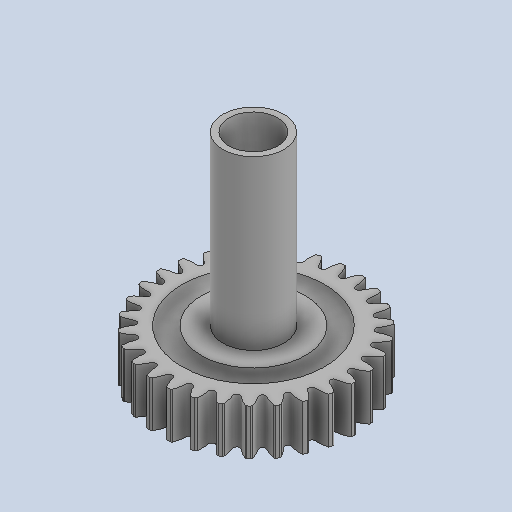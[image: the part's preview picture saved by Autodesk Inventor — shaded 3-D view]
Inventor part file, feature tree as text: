
AUTODESK INVENTOR PART (.ipt)
format: ipt  version: 2024 (Build 280153000, 153)  size: 743,936 bytes
history: native  units: mm
features: extrude x5, sketch x4, pattern_circular x2, fillet x1, revolve x1, plane x1, mirror x1, other x1, projected_geometry x1
ambient origin geometry x8: Origin, YZ Plane, XZ Plane, XY Plane, X Axis, Y Axis, Z Axis, Center Point
bodies: Body1 (feature_tree), Body2 (feature_tree)
feature tree (17):
  sketch  "Sketch4"  dims[d10=15.0mm d11=0.0mm d12=0.0mm d13=0.0mm]
  extrude  "Extrusion4"  TaperAngle=0.0deg  [1 undecoded]
  extrude  "Extrusion5"  Depth=0.5mm
  pattern_circular  "Circular Pattern1"  Count=30 Angle=360.0deg
  fillet  "Fillet1"  Radius=6.35mm
  pattern_circular  "Circular Pattern2"  Count=2  [1 undecoded]
  revolve  "Revolution1"  [1 undecoded]
  plane  "Work Plane1"
  mirror  "Mirror1"
  extrude  "Extrusion9"  Depth=55.0mm
  extrude  "Extrusion10"  Depth=55.0mm TaperAngle=0.0deg
  other  "Srf1"
  sketch  "Sketch8"  dims[d14=300.0mm d15=360.0deg d26=0.5mm d27=300.0mm d28=360.0deg d30=0.0mm d31=0.0mm d32=6.35mm d33=20.0mm]
  sketch  "Sketch9"  dims[d34=90.0deg d35=-7.5mm]
  sketch  "Sketch10"  dims[d36=20.0mm d37=2.0mm d38=55.0mm d39=0.0mm d40=0.0mm d41=0.0mm d42=0.5mm d43=0.872665mm d44=0.5mm d45=0.872665mm]
  projected_geometry  "Projected Loop1"
  extrude  "ExtrusionSrf1"  TaperAngle=0.0deg  [1 undecoded]
note: 4 required parameter values undecoded (feature->parameter linkage not recoverable at this tier; creation-order binding heuristic only, values carry confidence <= 0.55)